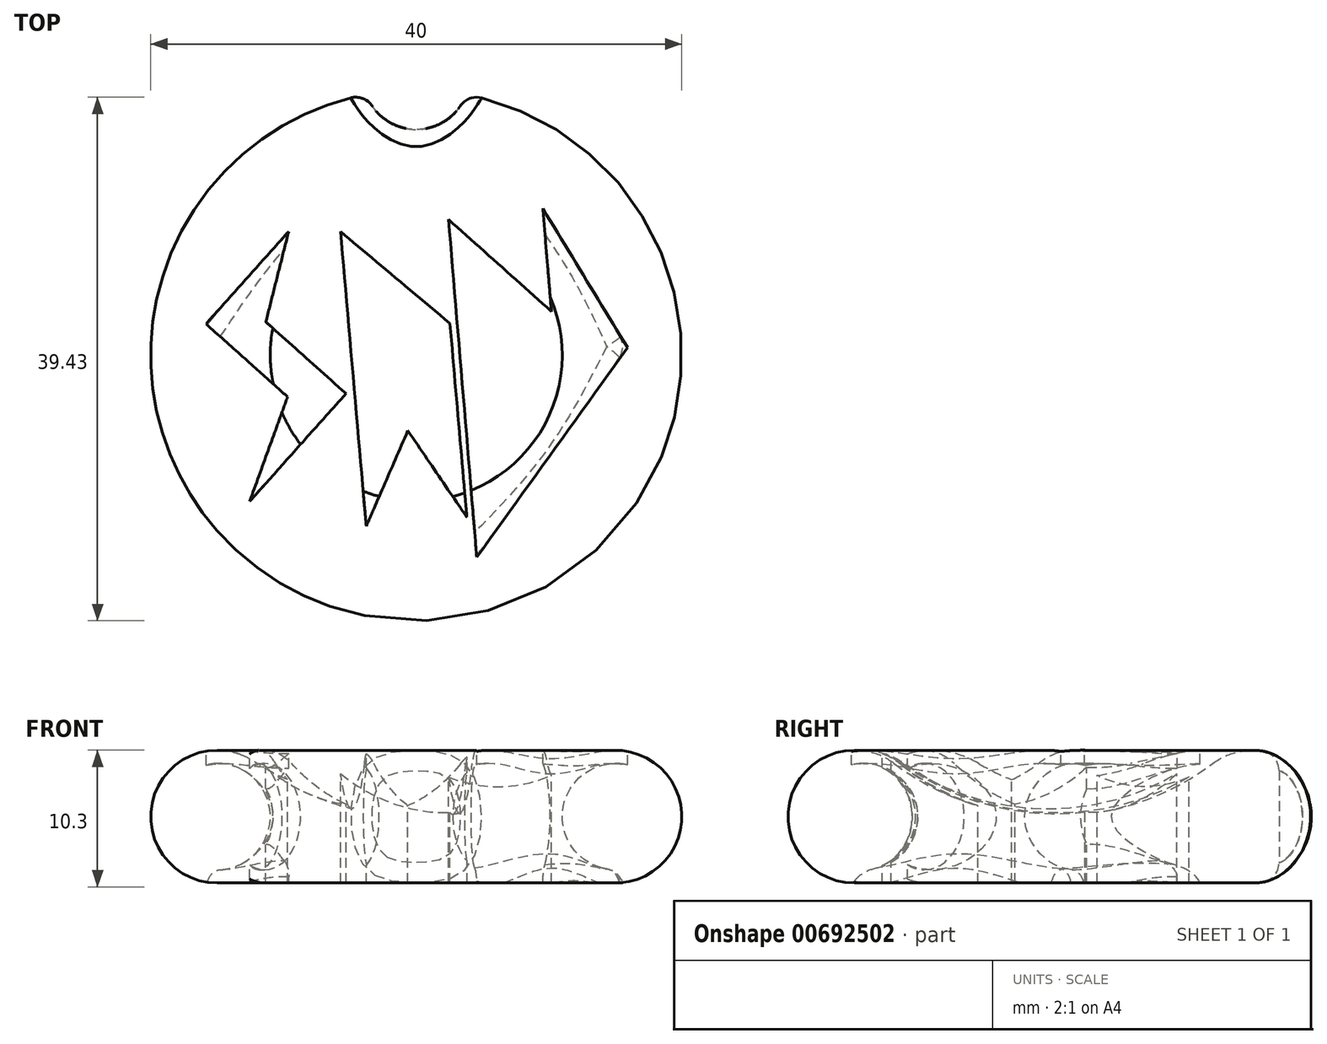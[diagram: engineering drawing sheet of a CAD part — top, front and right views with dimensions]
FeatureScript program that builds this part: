
annotation { "Feature Type Name" : "Feature", "Feature Type Description" : "" }
export const myFeature = defineFeature(function(context is Context, id is Id, definition is map)
    precondition{}
    {
        {
            var Q0;
            Q0=qCreatedBy(makeId("Front.planeOp"),FACE);
            var sketch = newSketch(context, id + "F0", { "sketchPlane" : qUnion([Q0])});
            skArc(sketch, "E0", {"start": v(-12, 9) * mm, "mid": v(-19.74, 6.58) * mm, "end": v(-15, 0) * mm});
            skArc(sketch, "E1", {"start": v(-12, 9) * mm, "mid": v(-6.32, 6.03) * mm, "end": v(0, 5) * mm});
            skLineSegment(sketch, "E2", {"start": v(0, 0) * mm, "end": v(-15, 0) * mm});
            skLineSegment(sketch, "E3", {"start": v(0, 0) * mm, "end": v(0, 5) * mm});
            skSolve(sketch);
        }
        {
            var Q0;
            Q0=makeQuery(id+"F0.imprint","IMPRINT",FACE,{"disambiguationData":[TD([[makeQuery(id+"F0.imprint","IMPRINT",EDGE,{"derivedFrom":sQuery(id+"F0.wireOp",EDGE,"E0")}),1.0]])]});
            var Q1;
            Q1=sQuery(id+"F0.wireOp",EDGE,"E3");
            revolve(context, id + "F1", {"entities" : qUnion([Q0]), "axis" : qUnion([Q1]), "revolveType" : RevolveType.FULL});
        }
        {
            var Q0;
            Q0=qCreatedBy(makeId("Top.planeOp"),FACE);
            cPlane(context, id + "F2", {"entities" : qUnion([Q0]), "cplaneType" : CPlaneType.OFFSET, "offset" : 10 * mm, "width" : 150 * mm, "height" : 150 * mm});
        }
        {
            var Q0;
            Q0=qCreatedBy(id+"F2.planeOp",FACE);
            var sketch = newSketch(context, id + "F3", { "sketchPlane" : qUnion([Q0])});
            skLineSegment(sketch, "E4", {"start": v(-11.33, 2.5) * mm, "end": v(-5.3, -2.9) * mm});
            skLineSegment(sketch, "E5", {"start": v(-5.3, -2.9) * mm, "end": v(-12.54, -11) * mm});
            skLineSegment(sketch, "E6", {"start": v(-12.54, -11) * mm, "end": v(-9.7, -3.14) * mm});
            skLineSegment(sketch, "E7", {"start": v(-9.7, -3.14) * mm, "end": v(-15.84, 2.36) * mm});
            skLineSegment(sketch, "E8", {"start": v(-15.84, 2.36) * mm, "end": v(-9.6, 9.32) * mm});
            skLineSegment(sketch, "E9", {"start": v(-11.33, 2.5) * mm, "end": v(-9.6, 9.32) * mm});
            skLineSegment(sketch, "E10", {"start": v(-4.26, -15.21) * mm, "end": v(-6.33, 9.52) * mm});
            skLineSegment(sketch, "E11", {"start": v(-6.33, 9.52) * mm, "end": v(3.2, 1) * mm});
            skLineSegment(sketch, "E12", {"start": v(3.2, 1) * mm, "end": v(4.56, -15.22) * mm});
            skLineSegment(sketch, "E13", {"start": v(4.56, -15.22) * mm, "end": v(0.05, -8.56) * mm});
            skLineSegment(sketch, "E14", {"start": v(0.05, -8.56) * mm, "end": v(-4.26, -15.21) * mm});
            skLineSegment(sketch, "E15", {"start": v(2.43, 10.22) * mm, "end": v(4.56, -15.22) * mm});
            skLineSegment(sketch, "E16", {"start": v(2.43, 10.22) * mm, "end": v(10.18, 3.29) * mm});
            skLineSegment(sketch, "E17", {"start": v(10.18, 3.29) * mm, "end": v(9.53, 11.05) * mm});
            skLineSegment(sketch, "E18", {"start": v(9.53, 11.05) * mm, "end": v(15.92, 0.56) * mm});
            skLineSegment(sketch, "E19", {"start": v(15.92, 0.56) * mm, "end": v(4.56, -15.22) * mm});
            skLineSegment(sketch, "E20.0", {"start": v(4.56, -15.22) * mm, "end": v(2.43, 10.22) * mm, "construction": true});
            skLineSegment(sketch, "E21.0", {"start": v(-4.26, -15.21) * mm, "end": v(-5.3, -2.9) * mm, "construction": true});
            skSolve(sketch);
        }
        {
            var Q0;
            Q0=makeQuery(id+"F3.imprint","IMPRINT",FACE,{"disambiguationData":[TD([[makeQuery(id+"F3.imprint","IMPRINT",EDGE,{"derivedFrom":sQuery(id+"F3.wireOp",EDGE,"E4")}),-1.0]])]});
            var Q1;
            {var subQ0=sQuery(id+"F3.wireOp",EDGE,"E16");Q1=makeQuery(id+"F3.imprint","IMPRINT",FACE,{"disambiguationData":[TD([[makeQuery(id+"F3.imprint","IMPRINT",EDGE,{"derivedFrom":subQ0}),-1.0]])]});}
            extrude(context, id + "F4", {"entities" : qUnion([Q0, Q1]), "operationType" : NewBodyOperationType.REMOVE, "oppositeDirection" : true, "depth" : 25 * mm, "offsetDistance" : 25 * mm});
        }
        {
            var Q0;
            Q0=qCreatedBy(id+"F2.planeOp",FACE);
            var sketch = newSketch(context, id + "F5", { "sketchPlane" : qUnion([Q0])});
            skLineSegment(sketch, "E22", {"start": v(-3.77, -12.89) * mm, "end": v(-5.7, 9.3) * mm});
            skLineSegment(sketch, "E23", {"start": v(-5.7, 9.3) * mm, "end": v(2.54, 2.39) * mm});
            skLineSegment(sketch, "E24", {"start": v(2.54, 2.39) * mm, "end": v(3.82, -12.22) * mm});
            skLineSegment(sketch, "E25", {"start": v(3.82, -12.22) * mm, "end": v(-0.63, -5.68) * mm});
            skLineSegment(sketch, "E26", {"start": v(-0.63, -5.68) * mm, "end": v(-3.77, -12.89) * mm});
            skLineSegment(sketch, "E27.0", {"start": v(-3.77, -12.89) * mm, "end": v(3.82, -12.22) * mm, "construction": true});
            skSolve(sketch);
        }
        {
            var Q0;
            Q0 = qSketchRegion(id + "F5", true);
            extrude(context, id + "F6", {"entities" : qUnion([Q0]), "operationType" : NewBodyOperationType.REMOVE, "oppositeDirection" : true, "depth" : 25 * mm, "offsetDistance" : 25 * mm});
        }
        {
            var Q0;
            Q0=qCreatedBy(makeId("Front.planeOp"),FACE);
            var sketch = newSketch(context, id + "F7", { "sketchPlane" : qUnion([Q0])});
            skCircle(sketch, "E28", {"center": v(-15, 5) * mm, "radius": 4 * mm});
            skSolve(sketch);
        }
        {
            var Q0;
            Q0 = qSketchRegion(id + "F7", true);
            var Q1;
            Q1=sQuery(id+"F0.wireOp",EDGE,"E3");
            revolve(context, id + "F8", {"operationType" : NewBodyOperationType.ADD, "entities" : qUnion([Q0]), "axis" : qUnion([Q1]), "revolveType" : RevolveType.FULL});
        }
        {
            var Q0;
            Q0=qCreatedBy(makeId("Top.planeOp"),FACE);
            var sketch = newSketch(context, id + "F9", { "sketchPlane" : qUnion([Q0])});
            skCircle(sketch, "E29", {"center": v(0, 21) * mm, "radius": 4 * mm});
            skSolve(sketch);
        }
        {
            var Q0;
            Q0 = qSketchRegion(id + "F9", true);
            extrude(context, id + "F10", {"entities" : qUnion([Q0]), "operationType" : NewBodyOperationType.REMOVE, "depth" : 18.8 * mm, "offsetDistance" : 25 * mm});
        }
        {
            var Q0;
            Q0=makeQuery(id+"F10.boolean.opBoolean","COPY",FACE,{"derivedFrom":makeQuery(id+"F10.opExtrude","SWEPT_FACE",FACE,{"disambiguationData":[OSD([sQuery(id+"F9.wireOp",EDGE,"E29")])]})});
            fillet(context, id + "F11", {"entities" : qUnion([Q0]), "radius" : 1.5 * mm, "tangentPropagation" : true, "allowEdgeOverflow" : false});
        }
        {
            var Q0;
            Q0=makeQuery(id+"F8.boolean.opBoolean","INTERSECT",EDGE,{"disambiguationData":[OD(0.0)],"derivedFrom":[makeQuery(id+"F4.boolean.opBoolean","COPY",FACE,{"derivedFrom":makeQuery(id+"F4.opExtrude","SWEPT_FACE",FACE,{"disambiguationData":[OSD([sQuery(id+"F3.wireOp",EDGE,"E18")])]})}),makeQuery(id+"F8.opRevolve","SWEPT_FACE",FACE,{"disambiguationData":[OSD([sQuery(id+"F7.wireOp",EDGE,"E28")])]})]});
            fillet(context, id + "F12", {"entities" : qUnion([Q0]), "radius" : 1.5 * mm, "tangentPropagation" : true, "allowEdgeOverflow" : false});
        }
        {
            var Q0;
            Q0=makeQuery(id+"F8.boolean.opBoolean","INTERSECT",EDGE,{"disambiguationData":[OD(0.0)],"derivedFrom":[makeQuery(id+"F4.boolean.opBoolean","COPY",FACE,{"derivedFrom":makeQuery(id+"F4.opExtrude","SWEPT_FACE",FACE,{"disambiguationData":[OSD([sQuery(id+"F3.wireOp",EDGE,"E19")])]})}),makeQuery(id+"F8.opRevolve","SWEPT_FACE",FACE,{"disambiguationData":[OSD([sQuery(id+"F7.wireOp",EDGE,"E28")])]})]});
            fillet(context, id + "F13", {"entities" : qUnion([Q0]), "radius" : 1.5 * mm, "tangentPropagation" : true, "allowEdgeOverflow" : false});
        }
        {
            var Q0;
            Q0=makeQuery(id+"F8.boolean.opBoolean","INTERSECT",EDGE,{"disambiguationData":[OD(0.0)],"derivedFrom":[makeQuery(id+"F4.boolean.opBoolean","COPY",FACE,{"derivedFrom":makeQuery(id+"F4.opExtrude","SWEPT_FACE",FACE,{"disambiguationData":[OSD([sQuery(id+"F3.wireOp",EDGE,"E8")])]})}),makeQuery(id+"F8.opRevolve","SWEPT_FACE",FACE,{"disambiguationData":[OSD([sQuery(id+"F7.wireOp",EDGE,"E28")])]})]});
            fillet(context, id + "F14", {"entities" : qUnion([Q0]), "radius" : 1.5 * mm, "tangentPropagation" : true, "allowEdgeOverflow" : false});
        }
    });
